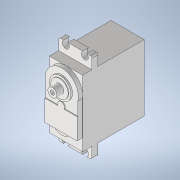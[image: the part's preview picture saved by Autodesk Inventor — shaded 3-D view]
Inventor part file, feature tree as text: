
AUTODESK INVENTOR PART (.ipt)
format: ipt  version: 2022 (Build 260153000, 153)  size: 237,056 bytes
history: native  units: mm
features: extrude x7, sketch x7, projected_geometry x4, fillet x1
ambient origin geometry x8: Origin, YZ Plane, XZ Plane, XY Plane, X Axis, Y Axis, Z Axis, Center Point
bodies: Solid1 (feature_tree)
feature tree (19):
  extrude  "Extrusion1"  Depth=54.0mm
  extrude  "Extrusion2"  Depth=28.0mm
  extrude  "Extrusion3"  Depth=3.6mm
  extrude  "Extrusion4"  Depth=20.0mm TaperAngle=0.0deg
  extrude  "Extrusion5"  Depth=2.6mm
  extrude  "Extrusion6"  Depth=20.6mm
  extrude  "Extrusion7"  Depth=3.6mm
  fillet  "Fillet1"  Radius=2.0mm
  sketch  "Sketch1"  dims[d0=38.0mm d1=54.0mm]
  sketch  "Sketch2"  dims[d3=40.0mm d4=28.0mm]
  projected_geometry  "Projected Loop1"
  sketch  "Sketch3"  dims[d5=47.2mm d6=3.6mm]
  sketch  "Sketch4"  dims[d7=5.65mm d8=20.0mm d9=0.0mm]
  projected_geometry  "Projected Loop4"
  sketch  "Sketch5"  dims[d11=9.7mm d12=2.6mm]
  sketch  "Sketch6"  dims[d13=6.0mm d14=20.6mm]
  sketch  "Sketch7"  dims[d15=2.5mm d16=0.0mm d19=9.0mm d20=2.0mm d21=12.7mm d25=2.1mm d26=3.75mm d27=0.5mm d28=0.0mm d29=13.0mm d30=1.0mm d31=0.0mm d32=10.5mm d33=0.4mm d34=0.0mm d35=5.5mm d36=2.6mm d37=4.3mm d38=0.0mm d39=3.0mm d40=2.5mm d42=2.15mm d44=2.5mm d45=2.15mm d46=4.3mm d47=0.0mm d48=1.0mm d49=28.0mm d50=5.65mm d51=3.6mm]
  projected_geometry  "Projected Loop5"
  projected_geometry  "Projected Loop6"
